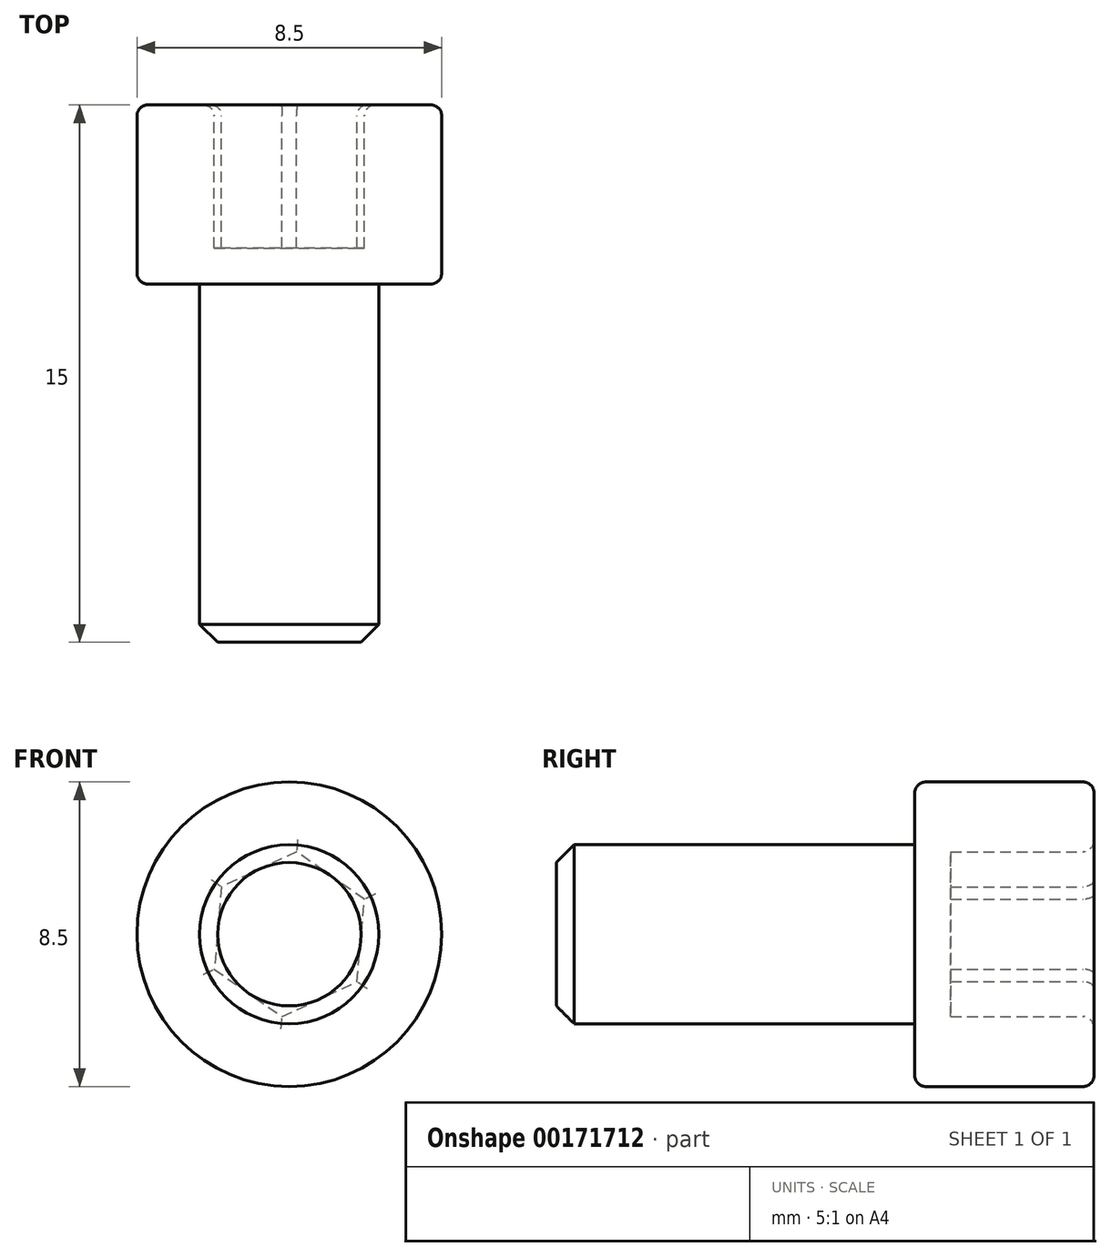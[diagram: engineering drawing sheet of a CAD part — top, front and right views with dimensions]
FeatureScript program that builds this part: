
annotation { "Feature Type Name" : "Feature", "Feature Type Description" : "" }
export const myFeature = defineFeature(function(context is Context, id is Id, definition is map)
    precondition{}
    {
        {
            var Q0;
            Q0=qCreatedBy(makeId("Front.planeOp"),FACE);
            var sketch = newSketch(context, id + "F0", { "sketchPlane" : qUnion([Q0])});
            skCircle(sketch, "E0", {"center": v(0, 0) * mm, "radius": 2.5 * mm});
            skSolve(sketch);
        }
        {
            var Q0;
            Q0=makeQuery(id+"F0.imprint","IMPRINT",FACE,{"disambiguationData":[TD([[makeQuery(id+"F0.imprint","IMPRINT",EDGE,{"derivedFrom":sQuery(id+"F0.wireOp",EDGE,"E0")}),1.0]])]});
            extrude(context, id + "F1", {"entities" : qUnion([Q0]), "depth" : 10 * mm});
        }
        {
            var Q0;
            Q0=makeQuery(id+"F1.opExtrude","CAP_EDGE",EDGE,{"disambiguationData":[OSD([sQuery(id+"F0.wireOp",EDGE,"E0")])],"isStart":false});
            chamfer(context, id + "F2", {"entities" : qUnion([Q0]), "width" : 0.5 * mm, "tangentPropagation" : true});
        }
        {
            var Q0;
            Q0=makeQuery(id+"F1.opExtrude","CAP_FACE",FACE,{"disambiguationData":[OSD([sQuery(id+"F0.wireOp",EDGE,"E0")])],"isStart":true});
            var sketch = newSketch(context, id + "F3", { "sketchPlane" : qUnion([Q0])});
            skCircle(sketch, "E1", {"center": v(0, 0) * mm, "radius": 4.25 * mm});
            skSolve(sketch);
        }
        {
            var Q0;
            Q0=makeQuery(id+"F3.imprint","IMPRINT",FACE,{"disambiguationData":[TD([[makeQuery(id+"F3.imprint","IMPRINT",EDGE,{"derivedFrom":sQuery(id+"F3.wireOp",EDGE,"E1")}),1.0]])]});
            var Q1;
            Q1=makeQuery(id+"F3.imprint","IMPRINT",FACE,{"disambiguationData":[TD([[makeQuery(id+"F3.imprint","IMPRINT",EDGE,{"derivedFrom":makeQuery(id+"F1.opExtrude","CAP_EDGE",EDGE,{"disambiguationData":[OSD([sQuery(id+"F0.wireOp",EDGE,"E0")])],"isStart":true})}),-1.0]])]});
            extrude(context, id + "F4", {"entities" : qUnion([Q0, Q1]), "operationType" : NewBodyOperationType.ADD, "depth" : 5 * mm});
        }
        {
            var Q0;
            Q0=makeQuery(id+"F4.opExtrude","CAP_FACE",FACE,{"disambiguationData":[OSD([sQuery(id+"F3.wireOp",EDGE,"E1")])],"isStart":false});
            var sketch = newSketch(context, id + "F5", { "sketchPlane" : qUnion([Q0])});
            skCircle(sketch, "E2.cCircle", {"center": v(0, 0) * mm, "radius": 2 * mm, "construction": true});
            skLineSegment(sketch, "E2.0", {"start": v(-2.1, 0.98) * mm, "end": v(-0.2, 2.3) * mm});
            skLineSegment(sketch, "E2.1", {"start": v(-0.2, 2.3) * mm, "end": v(1.9, 1.32) * mm});
            skLineSegment(sketch, "E2.2", {"start": v(1.9, 1.32) * mm, "end": v(2.1, -0.98) * mm});
            skLineSegment(sketch, "E2.3", {"start": v(2.1, -0.98) * mm, "end": v(0.2, -2.3) * mm});
            skLineSegment(sketch, "E2.4", {"start": v(0.2, -2.3) * mm, "end": v(-1.9, -1.32) * mm});
            skLineSegment(sketch, "E2.5", {"start": v(-1.9, -1.32) * mm, "end": v(-2.1, 0.98) * mm});
            skPoint(sketch, "E2.0.midPoint", {"position": v(-1.15, 1.64) * mm});
            skSolve(sketch);
        }
        {
            var Q0;
            Q0 = qSketchRegion(id + "F5", true);
            var Q1;
            Q1=makeQuery(id+"F5.imprint","IMPRINT",FACE,{"disambiguationData":[TD([[makeQuery(id+"F5.imprint","IMPRINT",EDGE,{"derivedFrom":sQuery(id+"F5.wireOp",EDGE,"E2.0")}),-1.0]])]});
            extrude(context, id + "F6", {"entities" : qUnion([Q0, Q1]), "operationType" : NewBodyOperationType.REMOVE, "oppositeDirection" : true, "depth" : 4 * mm});
        }
        {
            var Q0;
            Q0=makeQuery(id+"F4.opExtrude","CAP_EDGE",EDGE,{"disambiguationData":[OSD([sQuery(id+"F3.wireOp",EDGE,"E1")])],"isStart":false});
            var Q1;
            Q1=makeQuery(id+"F4.opExtrude","CAP_EDGE",EDGE,{"disambiguationData":[OSD([sQuery(id+"F3.wireOp",EDGE,"E1")])],"isStart":true});
            var Q2;
            Q2=makeQuery(id+"F6.boolean.opBoolean","COPY",EDGE,{"derivedFrom":makeQuery(id+"F6.opExtrude","CAP_EDGE",EDGE,{"disambiguationData":[OSD([sQuery(id+"F5.wireOp",EDGE,"E2.0")])],"isStart":true})});
            var Q3;
            Q3=makeQuery(id+"F6.boolean.opBoolean","COPY",EDGE,{"derivedFrom":makeQuery(id+"F6.opExtrude","CAP_EDGE",EDGE,{"disambiguationData":[OSD([sQuery(id+"F5.wireOp",EDGE,"E2.1")])],"isStart":true})});
            var Q4;
            Q4=makeQuery(id+"F4.opExtrude","CAP_FACE",FACE,{"disambiguationData":[OSD([sQuery(id+"F3.wireOp",EDGE,"E1")])],"isStart":false});
            var Q5;
            Q5=makeQuery(id+"F6.boolean.opBoolean","COPY",EDGE,{"derivedFrom":makeQuery(id+"F6.opExtrude","CAP_EDGE",EDGE,{"disambiguationData":[OSD([sQuery(id+"F5.wireOp",EDGE,"E2.3")])],"isStart":true})});
            fillet(context, id + "F7", {"entities" : qUnion([Q0, Q1, Q2, Q3, Q4, Q5]), "radius" : 0.3 * mm, "tangentPropagation" : true, "allowEdgeOverflow" : false});
        }
    });
